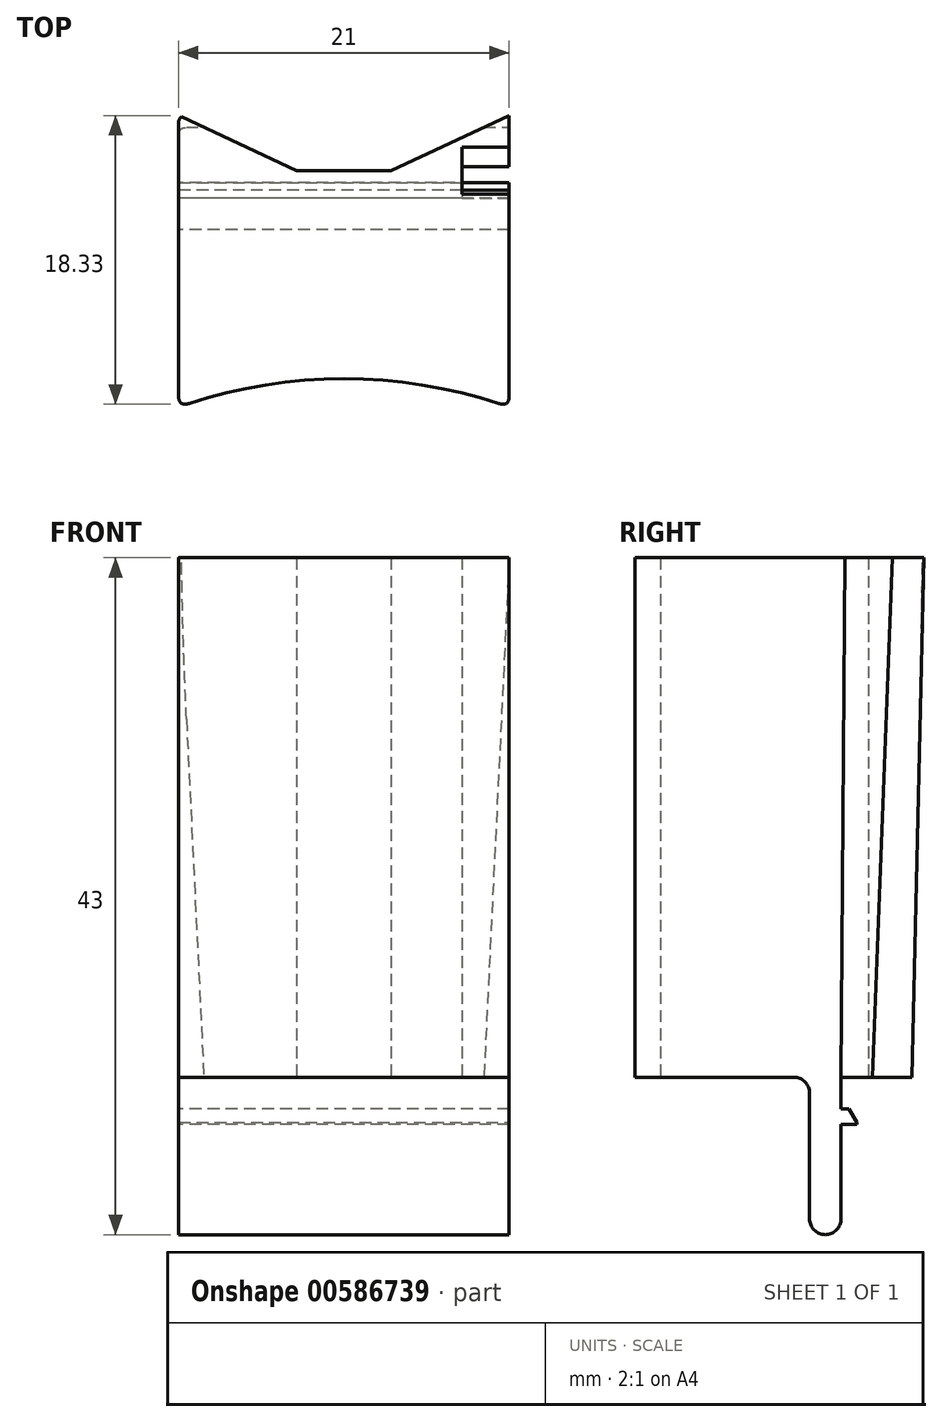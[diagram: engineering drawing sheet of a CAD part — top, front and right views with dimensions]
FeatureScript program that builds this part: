
annotation { "Feature Type Name" : "Feature", "Feature Type Description" : "" }
export const myFeature = defineFeature(function(context is Context, id is Id, definition is map)
    precondition{}
    {
        {
            var Q0;
            Q0=qCreatedBy(makeId("Top.planeOp"),FACE);
            var sketch = newSketch(context, id + "F0", { "sketchPlane" : qUnion([Q0])});
            skLineSegment(sketch, "E0.bottom", {"start": v(-33.95, 0) * mm, "end": v(-12.95, 0) * mm});
            skLineSegment(sketch, "E0.top", {"start": v(-33.95, 15) * mm, "end": v(-12.95, 15) * mm});
            skLineSegment(sketch, "E0.left", {"start": v(-33.95, 0) * mm, "end": v(-33.95, 15) * mm});
            skLineSegment(sketch, "E0.right", {"start": v(-12.95, 0) * mm, "end": v(-12.95, 15) * mm});
            skLineSegment(sketch, "E1", {"start": v(-33.95, 0) * mm, "end": v(-33.95, 37) * mm, "construction": true});
            skPoint(sketch, "E2", {"position": v(-23.45, 0) * mm});
            skLineSegment(sketch, "E3", {"start": v(-23.45, 0) * mm, "end": v(-23.45, 24.83) * mm, "construction": true});
            skLineSegment(sketch, "E4", {"start": v(-33.95, 15) * mm, "end": v(-33.95, 18.5) * mm});
            skLineSegment(sketch, "E5.MirrorCS", {"start": v(-12.95, 0) * mm, "end": v(-12.95, 37) * mm, "construction": true});
            skLineSegment(sketch, "E6", {"start": v(-12.95, 18.5) * mm, "end": v(-12.95, 15) * mm});
            skLineSegment(sketch, "E7", {"start": v(-33.95, 18.5) * mm, "end": v(-26.44, 15) * mm});
            skLineSegment(sketch, "E8.MirrorCS", {"start": v(-12.95, 18.5) * mm, "end": v(-20.45, 15) * mm});
            skArc(sketch, "E9", {"start": v(-12.95, 0) * mm, "mid": v(-23.45, 1.78) * mm, "end": v(-33.95, 0) * mm});
            skSolve(sketch);
        }
        {
            var Q0;
            {var subQ0=sQuery(id+"F0.wireOp",EDGE,"E4");Q0=makeQuery(id+"F0.imprint","IMPRINT",FACE,{"disambiguationData":[TD([[makeQuery(id+"F0.imprint","IMPRINT",EDGE,{"derivedFrom":subQ0}),-1.0]])]});}
            var Q1;
            {var subQ0=sQuery(id+"F0.wireOp",EDGE,"E6");Q1=makeQuery(id+"F0.imprint","IMPRINT",FACE,{"disambiguationData":[TD([[makeQuery(id+"F0.imprint","IMPRINT",EDGE,{"derivedFrom":subQ0}),-1.0]])]});}
            var Q2;
            {var subQ0=sQuery(id+"F0.wireOp",EDGE,"E0.left");Q2=makeQuery(id+"F0.imprint","IMPRINT",FACE,{"disambiguationData":[TD([[makeQuery(id+"F0.imprint","IMPRINT",EDGE,{"derivedFrom":subQ0}),-1.0]])]});}
            extrude(context, id + "F1", {"entities" : qUnion([Q0, Q1, Q2]), "depth" : 33 * mm, "offsetDistance" : 25 * mm});
        }
        {
            var Q0;
            Q0=makeQuery(id+"F1.opExtrude","SWEPT_FACE",FACE,{"disambiguationData":[OSD([sQuery(id+"F0.wireOp",EDGE,"E0.right"),sQuery(id+"F0.wireOp",EDGE,"E6")])]});
            var sketch = newSketch(context, id + "F2", { "sketchPlane" : qUnion([Q0])});
            skPoint(sketch, "E10", {"position": v(9.25, 33) * mm});
            skLineSegment(sketch, "E11", {"start": v(9.25, 33) * mm, "end": v(29.03, 33) * mm, "construction": true});
            skLineSegment(sketch, "E12", {"start": v(9.25, 33) * mm, "end": v(-16.64, 33) * mm, "construction": true});
            skLineSegment(sketch, "E13", {"start": v(18.5, 33) * mm, "end": v(17.75, 0) * mm});
            skPoint(sketch, "E14", {"position": v(18.5, 0) * mm});
            skLineSegment(sketch, "E15", {"start": v(18.5, 0) * mm, "end": v(17.75, 0) * mm});
            skLineSegment(sketch, "E16", {"start": v(18.5, 33) * mm, "end": v(18.5, 0) * mm});
            skPoint(sketch, "E17", {"position": v(15.25, 0) * mm});
            skPoint(sketch, "E18", {"position": v(16.5, 33) * mm});
            skLineSegment(sketch, "E19", {"start": v(16.5, 33) * mm, "end": v(15.25, 0) * mm});
            skPoint(sketch, "E20", {"position": v(13.5, 33) * mm});
            skLineSegment(sketch, "E21", {"start": v(13.5, 33) * mm, "end": v(13.25, 0) * mm});
            skLineSegment(sketch, "E22", {"start": v(16.5, 33) * mm, "end": v(13.5, 33) * mm});
            skLineSegment(sketch, "E23", {"start": v(-20.54, 10) * mm, "end": v(39.02, 10) * mm, "construction": true});
            skSolve(sketch);
        }
        {
            var Q0;
            Q0=makeQuery(id+"F2.imprint","IMPRINT",FACE,{"disambiguationData":[TD([[makeQuery(id+"F2.imprint","IMPRINT",EDGE,{"derivedFrom":sQuery(id+"F2.wireOp",EDGE,"E13")}),1.0]])]});
            extrude(context, id + "F3", {"entities" : qUnion([Q0]), "operationType" : NewBodyOperationType.REMOVE, "endBound" : BoundingType.THROUGH_ALL, "oppositeDirection" : true, "depth" : 25 * mm, "offsetDistance" : 25 * mm});
        }
        {
            var Q0;
            {var subQ0=sQuery(id+"F2.wireOp",EDGE,"E22");Q0=makeQuery(id+"F2.imprint","IMPRINT",FACE,{"disambiguationData":[TD([[makeQuery(id+"F2.imprint","IMPRINT",EDGE,{"derivedFrom":subQ0}),1.0]])]});}
            extrude(context, id + "F4", {"entities" : qUnion([Q0]), "operationType" : NewBodyOperationType.REMOVE, "oppositeDirection" : true, "depth" : 3 * mm, "offsetDistance" : 25 * mm});
        }
        {
            var Q0;
            {var subQ0=sQuery(id+"F0.wireOp",EDGE,"E0.bottom");var subQ3=sQuery(id+"F0.wireOp",EDGE,"E6");var subQ5=sQuery(id+"F0.wireOp",EDGE,"E0.right");Q0=makeQuery(id+"F4.boolean.opBoolean","SPLIT",FACE,{"disambiguationData":[TD([makeQuery(id+"F1.opExtrude","SWEPT_FACE",FACE,{"disambiguationData":[OSD([subQ0])]})])],"derivedFrom":makeQuery(id+"F1.opExtrude","SWEPT_FACE",FACE,{"disambiguationData":[OSD([subQ5,subQ3])]})});}
            var Q1;
            {var subQ0=sQuery(id+"F0.wireOp",EDGE,"E9");var subQ3=sQuery(id+"F0.wireOp",EDGE,"E6");var subQ5=sQuery(id+"F0.wireOp",EDGE,"E0.right");Q1=makeQuery(id+"F4.boolean.opBoolean","SPLIT",FACE,{"disambiguationData":[TD([makeQuery(id+"F1.opExtrude","SWEPT_FACE",FACE,{"disambiguationData":[OSD([subQ0])]})])],"derivedFrom":makeQuery(id+"F1.opExtrude","SWEPT_FACE",FACE,{"disambiguationData":[OSD([subQ5,subQ3])]})});}
            cPlane(context, id + "F5", {"entities" : qUnion([Q0, Q1]), "cplaneType" : CPlaneType.OFFSET, "offset" : 10.5 * mm, "oppositeDirection" : true, "width" : 150 * mm, "height" : 150 * mm});
        }
        {
            var Q0;
            Q0=makeQuery(id+"F3.boolean.opBoolean","COPY",EDGE,{"derivedFrom":makeQuery(id+"F3.opExtrude","CAP_EDGE",EDGE,{"disambiguationData":[OSD([sQuery(id+"F2.wireOp",EDGE,"E13")])],"isStart":true})});
            var Q1;
            Q1=makeQuery(id+"F3.boolean.opBoolean","INTERSECT",EDGE,{"derivedFrom":[makeQuery(id+"F1.opExtrude","SWEPT_FACE",FACE,{"disambiguationData":[OSD([sQuery(id+"F0.wireOp",EDGE,"E0.left"),sQuery(id+"F0.wireOp",EDGE,"E4")])]}),makeQuery(id+"F3.opExtrude","SWEPT_FACE",FACE,{"disambiguationData":[OSD([sQuery(id+"F2.wireOp",EDGE,"E13")])]})]});
            var Q2;
            Q2=makeQuery(id+"F1.opExtrude","SWEPT_EDGE",EDGE,{"disambiguationData":[OSD([sQuery(id+"F0.wireOp",EDGE,"E0.bottom"),sQuery(id+"F0.wireOp",EDGE,"E0.left")])]});
            var Q3;
            Q3=makeQuery(id+"F1.opExtrude","SWEPT_EDGE",EDGE,{"disambiguationData":[OSD([sQuery(id+"F0.wireOp",EDGE,"E0.bottom"),sQuery(id+"F0.wireOp",EDGE,"E0.right")])]});
            fillet(context, id + "F6", {"entities" : qUnion([Q0, Q1, Q2, Q3]), "radius" : 0.5 * mm, "tangentPropagation" : true, "rho" : 0.5, "crossSection" : FilletCrossSection.CONIC, "allowEdgeOverflow" : false});
        }
        {
            var Q0;
            Q0=makeQuery(id+"F1.opExtrude","CAP_FACE",FACE,{"disambiguationData":[OSD([sQuery(id+"F0.wireOp",EDGE,"E0.top"),sQuery(id+"F0.wireOp",EDGE,"E0.left"),sQuery(id+"F0.wireOp",EDGE,"E0.right"),sQuery(id+"F0.wireOp",EDGE,"E4"),sQuery(id+"F0.wireOp",EDGE,"E6"),sQuery(id+"F0.wireOp",EDGE,"E7"),sQuery(id+"F0.wireOp",EDGE,"E8.MirrorCS"),sQuery(id+"F0.wireOp",EDGE,"E9")])],"isStart":true});
            var sketch = newSketch(context, id + "F7", { "sketchPlane" : qUnion([Q0])});
            skLineSegment(sketch, "E24", {"start": v(-12.95, -11.25) * mm, "end": v(-33.95, -11.25) * mm});
            skLineSegment(sketch, "E25", {"start": v(-12.95, -13.25) * mm, "end": v(-33.95, -13.25) * mm});
            skLineSegment(sketch, "E26", {"start": v(-33.95, -13.25) * mm, "end": v(-33.95, -11.25) * mm});
            skLineSegment(sketch, "E27", {"start": v(-12.95, -13.25) * mm, "end": v(-12.95, -11.25) * mm});
            skSolve(sketch);
        }
        {
            var Q0;
            Q0 = qSketchRegion(id + "F7", true);
            extrude(context, id + "F8", {"entities" : qUnion([Q0]), "operationType" : NewBodyOperationType.ADD, "depth" : 10 * mm, "offsetDistance" : 25 * mm});
        }
        {
            var Q0;
            Q0=makeQuery(id+"F8.opExtrude","SWEPT_FACE",FACE,{"disambiguationData":[OSD([sQuery(id+"F7.wireOp",EDGE,"E25")])]});
            var sketch = newSketch(context, id + "F9", { "sketchPlane" : qUnion([Q0])});
            skLineSegment(sketch, "E28", {"start": v(12.95, -2) * mm, "end": v(33.95, -2) * mm});
            skLineSegment(sketch, "E29", {"start": v(12.95, -3) * mm, "end": v(33.95, -3) * mm});
            skLineSegment(sketch, "E30", {"start": v(33.95, -2) * mm, "end": v(33.95, -3) * mm});
            skLineSegment(sketch, "E31", {"start": v(12.95, -2) * mm, "end": v(12.95, -3) * mm});
            skSolve(sketch);
        }
        {
            var Q0;
            Q0=makeQuery(id+"F9.imprint","IMPRINT",FACE,{"disambiguationData":[TD([[makeQuery(id+"F9.imprint","IMPRINT",EDGE,{"derivedFrom":sQuery(id+"F9.wireOp",EDGE,"E28")}),-1.0]])]});
            extrude(context, id + "F10", {"entities" : qUnion([Q0]), "operationType" : NewBodyOperationType.ADD, "depth" : 1 * mm, "offsetDistance" : 25 * mm});
        }
        {
            var Q0;
            Q0=makeQuery(id+"F10.opExtrude","CAP_EDGE",EDGE,{"disambiguationData":[OSD([sQuery(id+"F9.wireOp",EDGE,"E28")])],"isStart":false});
            chamfer(context, id + "F11", {"entities" : qUnion([Q0]), "chamferType" : ChamferType.OFFSET_ANGLE, "width" : 0.5 * mm, "oppositeDirection" : false, "angle" : 60 * degree, "tangentPropagation" : true});
        }
        {
            var Q0;
            Q0=makeQuery(id+"F8.opExtrude","CAP_EDGE",EDGE,{"disambiguationData":[OSD([sQuery(id+"F7.wireOp",EDGE,"E24")])],"isStart":true});
            var Q1;
            Q1=makeQuery(id+"F8.opExtrude","CAP_EDGE",EDGE,{"disambiguationData":[OSD([sQuery(id+"F7.wireOp",EDGE,"E25")])],"isStart":false});
            var Q2;
            Q2=makeQuery(id+"F8.opExtrude","CAP_EDGE",EDGE,{"disambiguationData":[OSD([sQuery(id+"F7.wireOp",EDGE,"E24")])],"isStart":false});
            fillet(context, id + "F12", {"entities" : qUnion([Q0, Q1, Q2]), "radius" : 1 * mm, "tangentPropagation" : true, "allowEdgeOverflow" : false});
        }
    });
